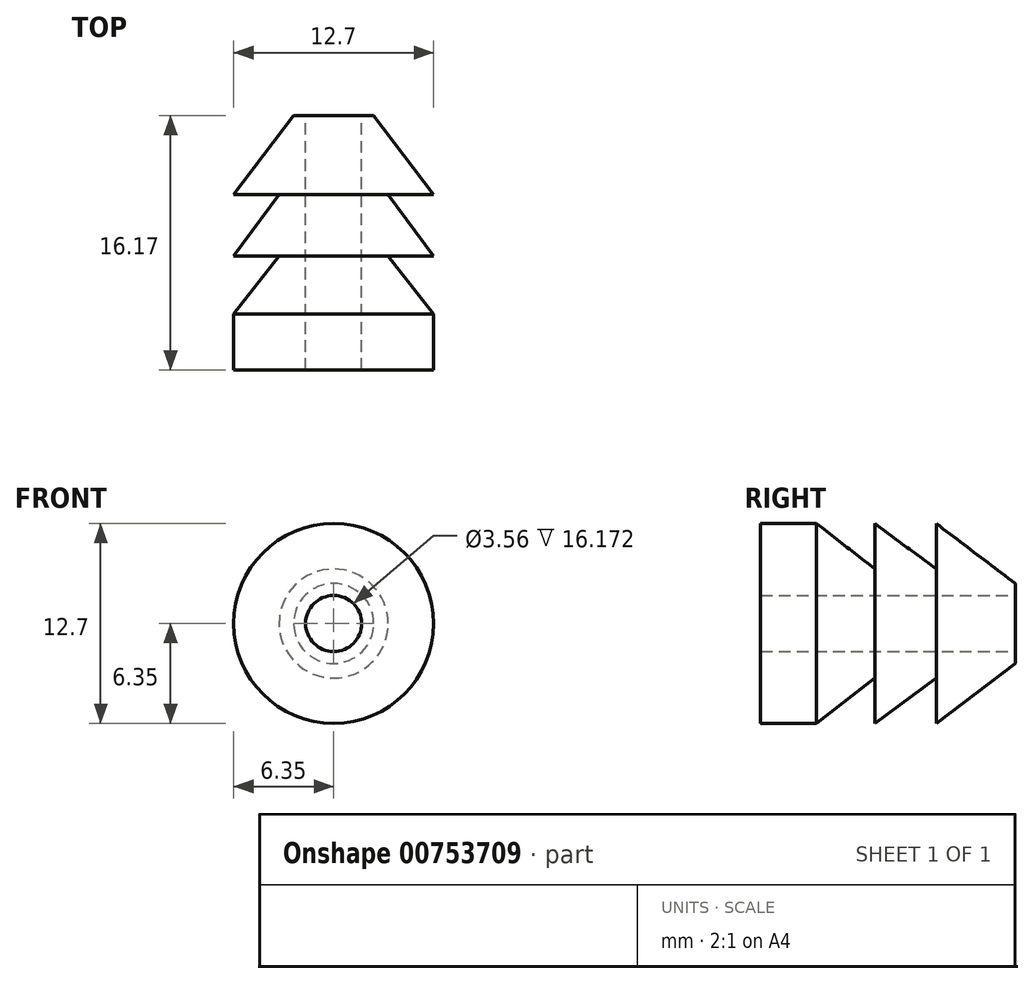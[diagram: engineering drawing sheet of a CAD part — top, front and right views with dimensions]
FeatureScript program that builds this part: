
annotation { "Feature Type Name" : "Feature", "Feature Type Description" : "" }
export const myFeature = defineFeature(function(context is Context, id is Id, definition is map)
    precondition{}
    {
        {
            var Q0;
            Q0=qCreatedBy(makeId("Right.planeOp"),FACE);
            var sketch = newSketch(context, id + "F0", { "sketchPlane" : qUnion([Q0])});
            skLineSegment(sketch, "E0", {"start": v(0, 0) * mm, "end": v(0, -6.35) * mm});
            skLineSegment(sketch, "E1", {"start": v(0, -6.35) * mm, "end": v(3.56, -6.35) * mm});
            skLineSegment(sketch, "E2", {"start": v(3.56, -6.35) * mm, "end": v(7.25, -3.46) * mm});
            skLineSegment(sketch, "E3", {"start": v(7.25, -3.46) * mm, "end": v(7.25, -6.35) * mm});
            skLineSegment(sketch, "E4", {"start": v(7.25, -6.35) * mm, "end": v(11.15, -3.46) * mm});
            skLineSegment(sketch, "E5", {"start": v(11.15, -3.46) * mm, "end": v(11.15, -6.35) * mm});
            skLineSegment(sketch, "E6", {"start": v(11.15, -6.35) * mm, "end": v(16.17, -2.54) * mm});
            skLineSegment(sketch, "E7", {"start": v(16.17, -2.54) * mm, "end": v(16.17, 0) * mm});
            skLineSegment(sketch, "E8", {"start": v(16.17, 0) * mm, "end": v(0, 0) * mm});
            skLineSegment(sketch, "E9", {"start": v(16.17, -1.78) * mm, "end": v(0, -1.78) * mm});
            skSolve(sketch);
        }
        {
            var Q0;
            {var subQ0=sQuery(id+"F0.wireOp",EDGE,"E1");Q0=makeQuery(id+"F0.imprint","IMPRINT",FACE,{"disambiguationData":[TD([[makeQuery(id+"F0.imprint","IMPRINT",EDGE,{"derivedFrom":subQ0}),1.0]])]});}
            var Q1;
            Q1=sQuery(id+"F0.wireOp",EDGE,"E8");
            revolve(context, id + "F1", {"surfaceOperationType" : NewSurfaceOperationType.NEW, "entities" : qUnion([Q0]), "axis" : qUnion([Q1]), "revolveType" : RevolveType.SYMMETRIC, "angle" : 360 * degree});
        }
    });
